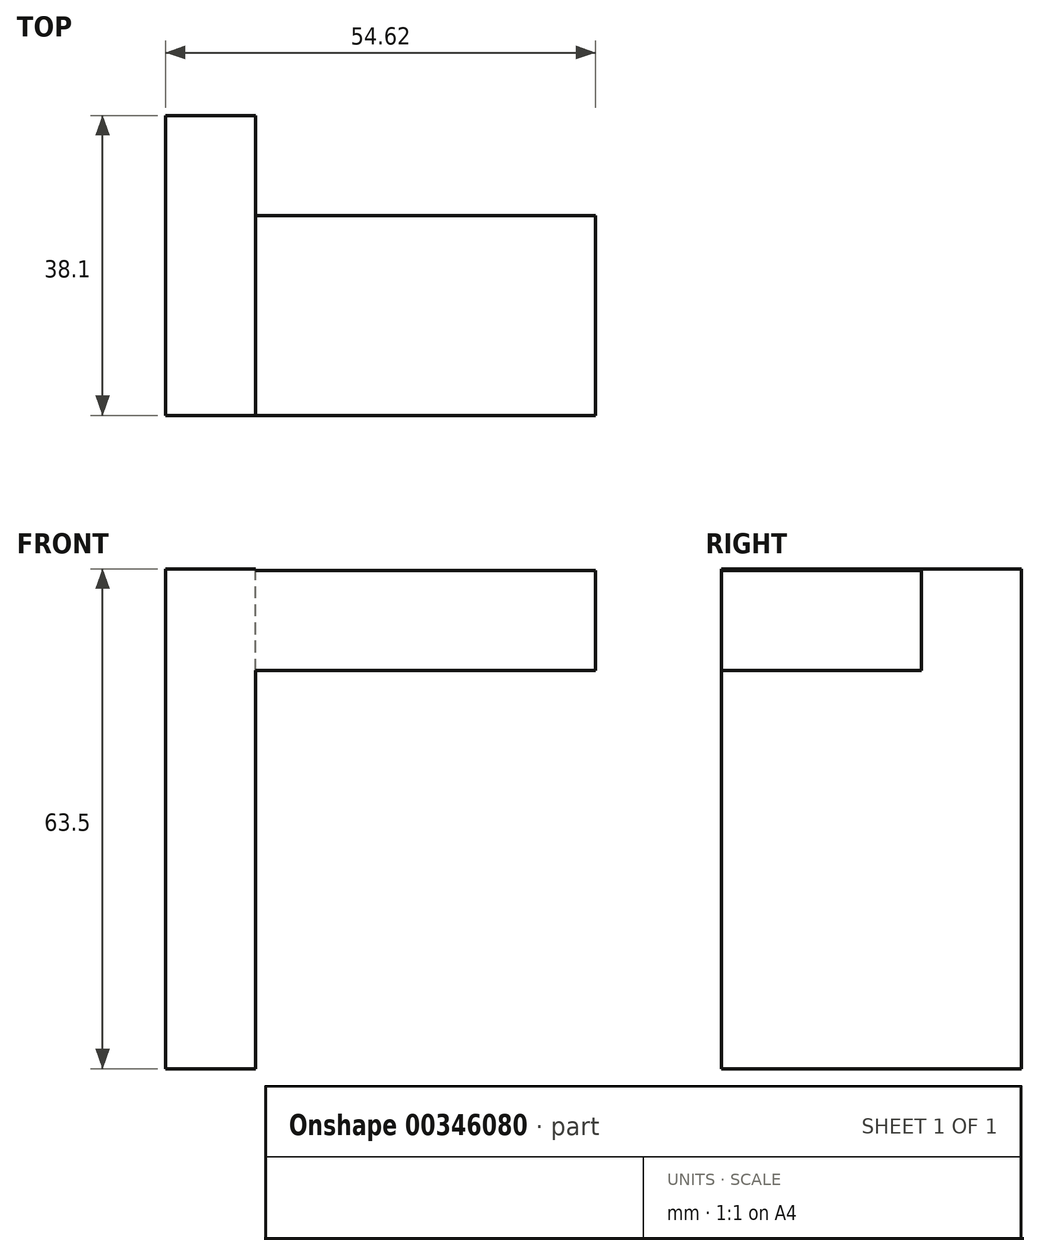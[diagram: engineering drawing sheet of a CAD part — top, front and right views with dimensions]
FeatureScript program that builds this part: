
annotation { "Feature Type Name" : "Feature", "Feature Type Description" : "" }
export const myFeature = defineFeature(function(context is Context, id is Id, definition is map)
    precondition{}
    {
        {
            var Q0;
            Q0=qCreatedBy(makeId("Front.planeOp"),FACE);
            var sketch = newSketch(context, id + "F0", { "sketchPlane" : qUnion([Q0])});
            skLineSegment(sketch, "E0.bottom", {"start": v(5.72, -31.75) * mm, "end": v(-5.72, -31.75) * mm});
            skLineSegment(sketch, "E0.top", {"start": v(5.72, 31.75) * mm, "end": v(-5.72, 31.75) * mm});
            skLineSegment(sketch, "E0.left", {"start": v(5.72, -31.75) * mm, "end": v(5.72, 31.75) * mm});
            skLineSegment(sketch, "E0.right", {"start": v(-5.72, -31.75) * mm, "end": v(-5.72, 31.75) * mm});
            skPoint(sketch, "E0.middle", {"position": v(0, 0) * mm});
            skLineSegment(sketch, "E1", {"start": v(5.72, 31.75) * mm, "end": v(5.72, 18.82) * mm});
            skLineSegment(sketch, "E2.bottom", {"start": v(5.72, 18.82) * mm, "end": v(5.92, 18.82) * mm});
            skLineSegment(sketch, "E2.top", {"start": v(5.72, 31.75) * mm, "end": v(5.72, 31.75) * mm});
            skLineSegment(sketch, "E2.left", {"start": v(5.72, 18.82) * mm, "end": v(5.72, 31.75) * mm});
            skLineSegment(sketch, "E3.bottom", {"start": v(5.72, 18.82) * mm, "end": v(48.9, 18.82) * mm});
            skLineSegment(sketch, "E3.top", {"start": v(5.72, 31.52) * mm, "end": v(48.9, 31.52) * mm});
            skLineSegment(sketch, "E3.left", {"start": v(5.72, 18.82) * mm, "end": v(5.72, 31.52) * mm});
            skLineSegment(sketch, "E3.right", {"start": v(48.9, 18.82) * mm, "end": v(48.9, 31.52) * mm});
            skSolve(sketch);
        }
        {
            var Q0;
            Q0=makeQuery(id+"F0.imprint","IMPRINT",FACE,{"disambiguationData":[TD([[makeQuery(id+"F0.imprint","IMPRINT",EDGE,{"derivedFrom":sQuery(id+"F0.wireOp",EDGE,"E0.bottom")}),-1.0]])]});
            extrude(context, id + "F1", {"entities" : qUnion([Q0]), "endBound" : BoundingType.SYMMETRIC, "depth" : 25.4 * mm});
        }
        {
            var Q0;
            Q0 = qSketchRegion(id + "F0", true);
            extrude(context, id + "F2", {"entities" : qUnion([Q0]), "operationType" : NewBodyOperationType.ADD, "depth" : 25.4 * mm});
        }
    });
